# Revit family: VSX09P_DN15_PN16_RFA_2018
name_source: partatom
category: Pipe Accessories
revit_build: Autodesk Revit LT 2018 (Build: 20180329_1100(x64)
units: mm (PartAtom-declared; Revit-internal decimal feet)

## family parameters
Always vertical = Yes
Cut with Voids When Loaded = No
Part Type = Valve - Breaks Into
Round Connector Dimension = Use Diameter
Shared = No
Work Plane-Based = No

## types (8) — shared parameters
CAT0 = Yes
E = 16 mm  [stored 0.0524934 ft]
H1 = 23 mm  [stored 0.0754593 ft]
L2D = 38 mm  [stored 0.124672 ft]
L2D_Min = 3048 mm  [stored 10 ft]
Manufacturer = Hydronix
QmdConnectorList = 301;D;302;D
R10 = 8 mm  [stored 0.0262467 ft]
R3 = 4 mm  [stored 0.0131234 ft]
R4 = 6 mm  [stored 0.019685 ft]
R5 = 7 mm  [stored 0.0229659 ft]
R8 = 2 mm  [stored 0.00656168 ft]
R9 = 9 mm  [stored 0.0295276 ft]
Type Comments = Závitový, vnější závit, ploché těsnění; LIN charakteristika; PN16; +5~+95°C; max.rychlost proudění 3,0 m/s
URL = www.hydronix.cz
W2D = 15 mm  [stored 0.0492126 ft]
X4 = 7 mm  [stored 0.0229659 ft]
X4__ve = -7 mm  [stored -0.0229659 ft]
Z2 = 5 mm  [stored 0.0164042 ft]
Z3 = 2 mm  [stored 0.00656168 ft]
Z5 = 9 mm  [stored 0.0295276 ft]
Z7 = 3 mm  [stored 0.00984252 ft]
Z7__ve = -3 mm
Z8 = 4 mm  [stored 0.0131234 ft]
magiPartTypeId = 306

## per-type parameters (varying)
| type | C | D | DT2 | Description | H | LT2 | MC Product Code | R1 | R2 | R6 | R7 | X3 | Z1 |
| VSX09P G1/2  PN16 kvs0,25 | 23 mm  [stored 0.0754593 ft] | 15 mm | 8 mm  [stored 0.0262467 ft] | 2 cestný regulační ventil malých spotřebičů, DN15; zdvih 2,5mm; max dp 250kPa; kvs0,25 | 27 mm  [stored 0.0885827 ft] | 19 mm  [stored 0.062336 ft] | VSX09P (G1/2"; dpmax=250kPa; kvs 0,25) | 7 mm  [stored 0.0229659 ft] | 13 mm | 11 mm | 15 mm  [stored 0.0492126 ft] | 34 mm  [stored 0.111549 ft] | 3 mm  [stored 0.00984252 ft] |
| VSX10P G1/2  PN16 kvs0,4 | 23 mm  [stored 0.0754593 ft] | 15 mm | 8 mm  [stored 0.0262467 ft] | 2 cestný regulační ventil malých spotřebičů, DN15; zdvih 2,5mm; max dp 250kPa; kvs0,4 | 27 mm  [stored 0.0885827 ft] | 19 mm  [stored 0.062336 ft] | VSX10P (G1/2"; dpmax=250kPa; kvs 0,4) | 7 mm  [stored 0.0229659 ft] | 13 mm | 11 mm | 15 mm  [stored 0.0492126 ft] | 34 mm  [stored 0.111549 ft] | 3 mm  [stored 0.00984252 ft] |
| VSX11P G1/2  PN16 kvs0,6 | 23 mm  [stored 0.0754593 ft] | 15 mm | 8 mm  [stored 0.0262467 ft] | 2 cestný regulační ventil malých spotřebičů, DN15; zdvih 2,5mm; max dp 250kPa; kvs0,6 | 27 mm  [stored 0.0885827 ft] | 19 mm  [stored 0.062336 ft] | VSX11P (G1/2"; dpmax=250kPa; kvs 0,6) | 7 mm  [stored 0.0229659 ft] | 13 mm | 11 mm | 15 mm  [stored 0.0492126 ft] | 34 mm  [stored 0.111549 ft] | 3 mm  [stored 0.00984252 ft] |
| VSX12P G1/2  PN16 kvs1,0 | 23 mm  [stored 0.0754593 ft] | 15 mm | 8 mm  [stored 0.0262467 ft] | 2 cestný regulační ventil malých spotřebičů, DN15; zdvih 2,5mm; max dp 250kPa; kvs1,0 | 27 mm  [stored 0.0885827 ft] | 19 mm  [stored 0.062336 ft] | VSX12P (G1/2"; dpmax=250kPa; kvs 1,0) | 7 mm  [stored 0.0229659 ft] | 13 mm | 11 mm | 15 mm  [stored 0.0492126 ft] | 34 mm  [stored 0.111549 ft] | 3 mm  [stored 0.00984252 ft] |
| VSX13P G1/2  PN16 kvs1,6 | 23 mm  [stored 0.0754593 ft] | 15 mm | 8 mm  [stored 0.0262467 ft] | 2 cestný regulační ventil malých spotřebičů, DN15; zdvih 2,5mm; max dp 250kPa; kvs1,6 | 27 mm  [stored 0.0885827 ft] | 19 mm  [stored 0.062336 ft] | VSX13P (G1/2"; dpmax=250kPa; kvs 1,6) | 7 mm  [stored 0.0229659 ft] | 13 mm | 11 mm | 15 mm  [stored 0.0492126 ft] | 34 mm  [stored 0.111549 ft] | 3 mm  [stored 0.00984252 ft] |
| VSX21P G3/4  PN16 kvs2,5 | 24 mm  [stored 0.0787402 ft] | 20 mm | 10 mm  [stored 0.0328084 ft] | 2 cestný regulační ventil malých spotřebičů, DN20; zdvih 2,5mm; max dp 150kPa; kvs2,5 | 26 mm  [stored 0.0853018 ft] | 21 mm  [stored 0.0688976 ft] | VSX21P (G3/4"; dpmax=150kPa; kvs 2,5) | 9 mm  [stored 0.0295276 ft] | 15 mm  [stored 0.0492126 ft] | 12 mm  [stored 0.0393701 ft] | 16 mm  [stored 0.0524934 ft] | 38 mm  [stored 0.124672 ft] | 4 mm  [stored 0.0131234 ft] |
| VSX24P G3/4  PN16 kvs4,0 | 24 mm  [stored 0.0787402 ft] | 20 mm | 10 mm  [stored 0.0328084 ft] | 2 cestný regulační ventil malých spotřebičů, DN20; zdvih 2,5mm; max dp 150kPa; kvs4,0 | 26 mm  [stored 0.0853018 ft] | 21 mm  [stored 0.0688976 ft] | VSX24P (G3/4"; dpmax=150kPa; kvs 4,0) | 9 mm  [stored 0.0295276 ft] | 15 mm  [stored 0.0492126 ft] | 12 mm  [stored 0.0393701 ft] | 16 mm  [stored 0.0524934 ft] | 38 mm  [stored 0.124672 ft] | 4 mm  [stored 0.0131234 ft] |
| VSX26P G3/4  PN16 kvs6,0 | 24 mm  [stored 0.0787402 ft] | 20 mm | 10 mm  [stored 0.0328084 ft] | 2 cestný regulační ventil malých spotřebičů, DN20; zdvih 2,5mm; max dp 150kPa; kvs6,0 | 26 mm  [stored 0.0853018 ft] | 21 mm  [stored 0.0688976 ft] | VSX26P (G3/4"; dpmax=150kPa; kvs 6,0) | 9 mm  [stored 0.0295276 ft] | 15 mm  [stored 0.0492126 ft] | 12 mm  [stored 0.0393701 ft] | 16 mm  [stored 0.0524934 ft] | 38 mm  [stored 0.124672 ft] | 4 mm  [stored 0.0131234 ft] |

note: [stored X ft] marks values corroborated as IEEE doubles in the binary element streams (Revit-internal decimal feet)

## geometry (parser evidence)
native form markers: Sweep x1
no freeform markers — native parametric forms only
